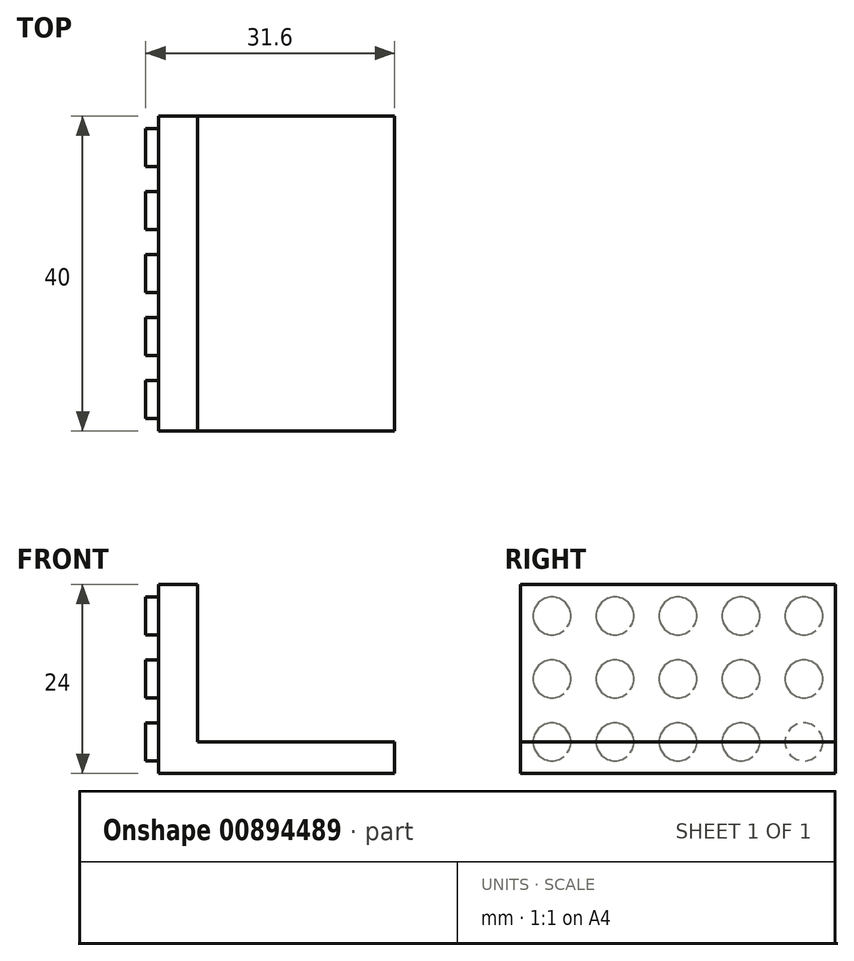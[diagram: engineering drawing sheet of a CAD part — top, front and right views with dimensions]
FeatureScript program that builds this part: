
annotation { "Feature Type Name" : "Feature", "Feature Type Description" : "" }
export const myFeature = defineFeature(function(context is Context, id is Id, definition is map)
    precondition{}
    {
        {
            var Q0;
            Q0=qCreatedBy(makeId("Top.planeOp"),FACE);
            var sketch = newSketch(context, id + "F0", { "sketchPlane" : qUnion([Q0])});
            skLineSegment(sketch, "E0.bottom", {"start": v(15, 20) * mm, "end": v(-15, 20) * mm});
            skLineSegment(sketch, "E0.top", {"start": v(15, -20) * mm, "end": v(-15, -20) * mm});
            skLineSegment(sketch, "E0.left", {"start": v(15, 20) * mm, "end": v(15, -20) * mm});
            skLineSegment(sketch, "E0.right", {"start": v(-15, 20) * mm, "end": v(-15, -20) * mm});
            skPoint(sketch, "E0.middle", {"position": v(0, 0) * mm});
            skSolve(sketch);
        }
        {
            var Q0;
            Q0 = qSketchRegion(id + "F0", true);
            extrude(context, id + "F1", {"entities" : qUnion([Q0]), "depth" : 24 * mm, "offsetDistance" : 25 * mm});
        }
        {
            var Q0;
            Q0=makeQuery(id+"F1.opExtrude","CAP_FACE",FACE,{"disambiguationData":[OSD([sQuery(id+"F0.wireOp",EDGE,"E0.bottom"),sQuery(id+"F0.wireOp",EDGE,"E0.top"),sQuery(id+"F0.wireOp",EDGE,"E0.left"),sQuery(id+"F0.wireOp",EDGE,"E0.right")])],"isStart":false});
            var sketch = newSketch(context, id + "F2", { "sketchPlane" : qUnion([Q0])});
            skLineSegment(sketch, "E1.bottom", {"start": v(15, -20) * mm, "end": v(-10, -20) * mm});
            skLineSegment(sketch, "E1.top", {"start": v(15, 20) * mm, "end": v(-10, 20) * mm});
            skLineSegment(sketch, "E1.left", {"start": v(15, -20) * mm, "end": v(15, 20) * mm});
            skLineSegment(sketch, "E1.right", {"start": v(-10, -20) * mm, "end": v(-10, 20) * mm});
            skSolve(sketch);
        }
        {
            var Q0;
            Q0=makeQuery(id+"F2.imprint","IMPRINT",FACE,{"disambiguationData":[TD([[makeQuery(id+"F2.imprint","IMPRINT",EDGE,{"derivedFrom":sQuery(id+"F2.wireOp",EDGE,"E1.bottom")}),-1.0]])]});
            extrude(context, id + "F3", {"entities" : qUnion([Q0]), "operationType" : NewBodyOperationType.REMOVE, "oppositeDirection" : true, "depth" : 20 * mm, "offsetDistance" : 25 * mm});
        }
        {
            var Q0;
            Q0=makeQuery(id+"F1.opExtrude","SWEPT_FACE",FACE,{"disambiguationData":[OSD([sQuery(id+"F0.wireOp",EDGE,"E0.right")])]});
            var sketch = newSketch(context, id + "F4", { "sketchPlane" : qUnion([Q0])});
            skCircle(sketch, "E2", {"center": v(-16, 4) * mm, "radius": 2.4 * mm});
            skCircle(sketch, "E3.0.1.0", {"center": v(-16, 12) * mm, "radius": 2.4 * mm});
            skCircle(sketch, "E3.0.2.0", {"center": v(-16, 20) * mm, "radius": 2.4 * mm});
            skCircle(sketch, "E3.1.0.0", {"center": v(-8, 4) * mm, "radius": 2.4 * mm});
            skCircle(sketch, "E3.1.1.0", {"center": v(-8, 12) * mm, "radius": 2.4 * mm});
            skCircle(sketch, "E3.1.2.0", {"center": v(-8, 20) * mm, "radius": 2.4 * mm});
            skCircle(sketch, "E3.2.0.0", {"center": v(0, 4) * mm, "radius": 2.4 * mm});
            skCircle(sketch, "E3.2.1.0", {"center": v(0, 12) * mm, "radius": 2.4 * mm});
            skCircle(sketch, "E3.2.2.0", {"center": v(0, 20) * mm, "radius": 2.4 * mm});
            skCircle(sketch, "E3.3.0.0", {"center": v(8, 4) * mm, "radius": 2.4 * mm});
            skCircle(sketch, "E3.3.1.0", {"center": v(8, 12) * mm, "radius": 2.4 * mm});
            skCircle(sketch, "E3.3.2.0", {"center": v(8, 20) * mm, "radius": 2.4 * mm});
            skCircle(sketch, "E3.4.0.0", {"center": v(16, 4) * mm, "radius": 2.4 * mm});
            skCircle(sketch, "E3.4.1.0", {"center": v(16, 12) * mm, "radius": 2.4 * mm});
            skCircle(sketch, "E3.4.2.0", {"center": v(16, 20) * mm, "radius": 2.4 * mm});
            skLineSegment(sketch, "E3.direction1", {"start": v(-16, 4) * mm, "end": v(-8, 4) * mm, "construction": true});
            skLineSegment(sketch, "E3.direction2", {"start": v(-16, 4) * mm, "end": v(-16, 12) * mm, "construction": true});
            skSolve(sketch);
        }
        {
            var Q0;
            Q0 = qSketchRegion(id + "F4", true);
            extrude(context, id + "F5", {"entities" : qUnion([Q0]), "operationType" : NewBodyOperationType.ADD, "depth" : 1.6 * mm, "offsetDistance" : 25 * mm});
        }
    });
